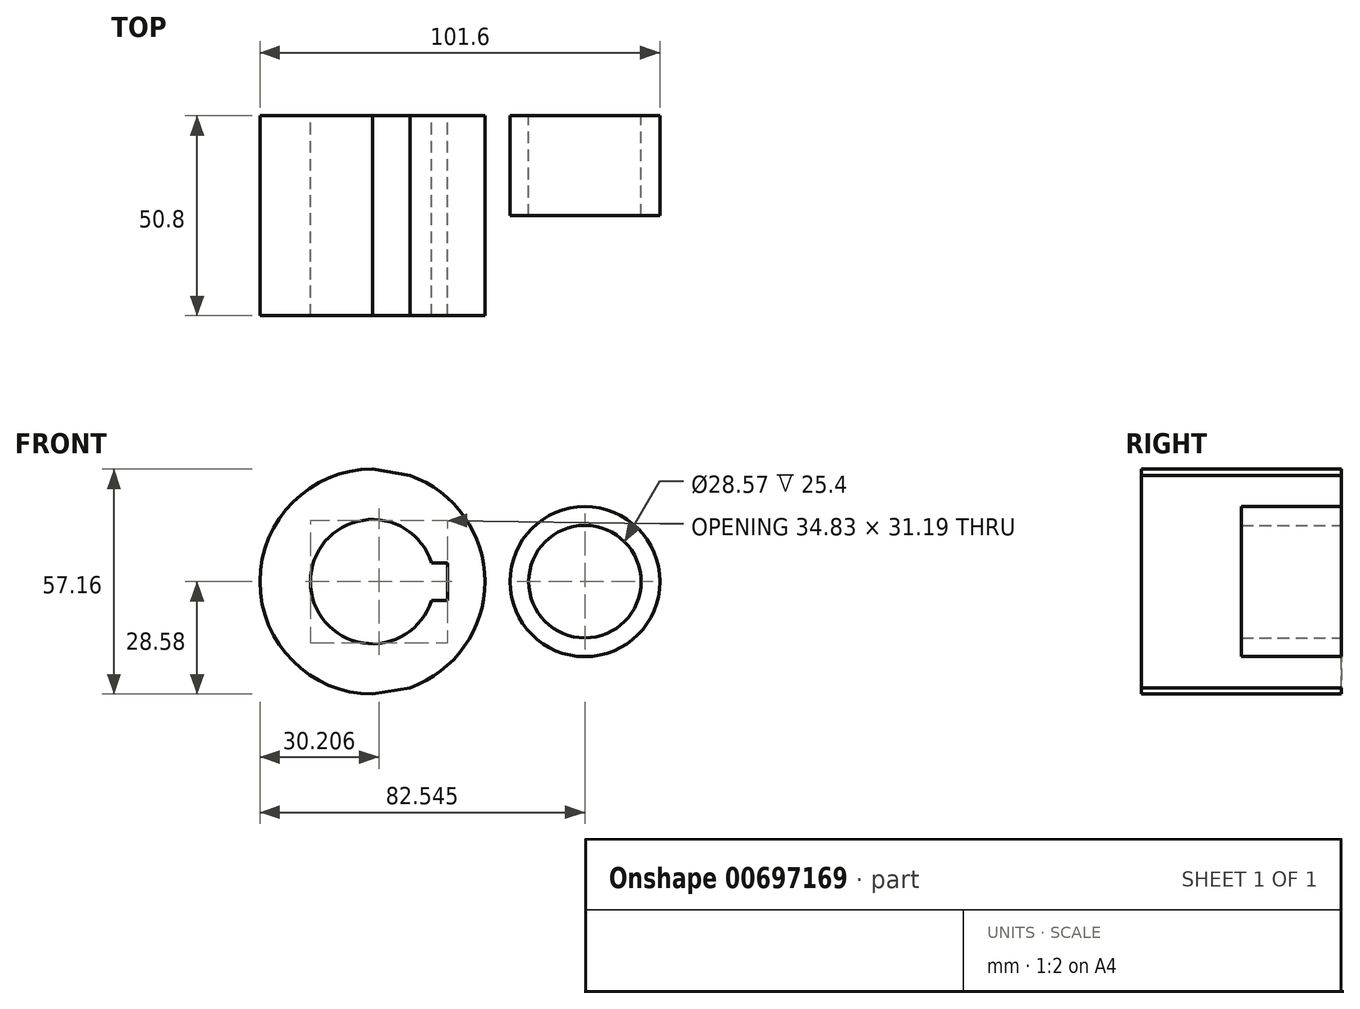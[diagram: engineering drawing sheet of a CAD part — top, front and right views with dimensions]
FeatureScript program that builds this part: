
annotation { "Feature Type Name" : "Feature", "Feature Type Description" : "" }
export const myFeature = defineFeature(function(context is Context, id is Id, definition is map)
    precondition{}
    {
        {
            var Q0;
            Q0=qCreatedBy(makeId("Front.planeOp"),FACE);
            var sketch = newSketch(context, id + "F0", { "sketchPlane" : qUnion([Q0])});
            skCircle(sketch, "E0", {"center": v(0, 0) * mm, "radius": 28.58 * mm});
            skCircle(sketch, "E1", {"center": v(53.97, 0) * mm, "radius": 19.05 * mm});
            skLineSegment(sketch, "E2", {"start": v(0, 28.57) * mm, "end": v(57.2, 18.78) * mm});
            skLineSegment(sketch, "E3", {"start": v(0, -28.58) * mm, "end": v(57.2, -18.78) * mm});
            skCircle(sketch, "E4", {"center": v(0, 0) * mm, "radius": 15.78 * mm});
            skCircle(sketch, "E5", {"center": v(53.97, 0) * mm, "radius": 14.29 * mm});
            skLineSegment(sketch, "E6.bottom", {"start": v(-19.05, -4.76) * mm, "end": v(19.05, -4.76) * mm});
            skLineSegment(sketch, "E6.top", {"start": v(-19.05, 4.76) * mm, "end": v(19.05, 4.76) * mm});
            skLineSegment(sketch, "E6.left", {"start": v(-19.05, -4.76) * mm, "end": v(-19.05, 4.76) * mm});
            skLineSegment(sketch, "E6.right", {"start": v(19.05, -4.76) * mm, "end": v(19.05, 4.76) * mm});
            skSolve(sketch);
        }
        {
            var Q0;
            {var subQ4=sQuery(id+"F0.wireOp",EDGE,"E6.left");Q0=makeQuery(id+"F0.imprint","IMPRINT",FACE,{"disambiguationData":[TD([[makeQuery(id+"F0.imprint","IMPRINT",EDGE,{"derivedFrom":subQ4}),1.0]])]});}
            var Q1;
            {var subQ0=sQuery(id+"F0.wireOp",EDGE,"E2");var subQ1=sQuery(id+"F0.wireOp",EDGE,"E0");var subQ2=makeQuery(id+"F0.imprint","INTERSECT",VERTEX,{"disambiguationData":[OD(1.0)],"derivedFrom":[subQ1,subQ0]});Q1=makeQuery(id+"F0.imprint","IMPRINT",FACE,{"disambiguationData":[TD([[makeQuery(id+"F0.imprint","IMPRINT",EDGE,{"disambiguationData":[TD([[subQ2,1.0]])],"derivedFrom":subQ1}),-1.0]])]});}
            var Q2;
            Q2=makeQuery(id+"F0.imprint","IMPRINT",FACE,{"disambiguationData":[TD([[makeQuery(id+"F0.imprint","IMPRINT",EDGE,{"derivedFrom":sQuery(id+"F0.wireOp",EDGE,"E5")}),-1.0]])]});
            var Q3;
            {var subQ5=sQuery(id+"F0.wireOp",EDGE,"E6.left");Q3=makeQuery(id+"F0.imprint","IMPRINT",FACE,{"disambiguationData":[TD([[makeQuery(id+"F0.imprint","IMPRINT",EDGE,{"derivedFrom":subQ5}),-1.0]])]});}
            extrude(context, id + "F1", {"entities" : qUnion([Q0, Q1, Q2, Q3]), "depth" : 25.4 * mm, "offsetDistance" : 25.4 * mm});
        }
        {
            var Q0;
            {var subQ4=sQuery(id+"F0.wireOp",EDGE,"E6.left");Q0=makeQuery(id+"F0.imprint","IMPRINT",FACE,{"disambiguationData":[TD([[makeQuery(id+"F0.imprint","IMPRINT",EDGE,{"derivedFrom":subQ4}),1.0]])]});}
            var Q1;
            {var subQ5=sQuery(id+"F0.wireOp",EDGE,"E6.left");Q1=makeQuery(id+"F0.imprint","IMPRINT",FACE,{"disambiguationData":[TD([[makeQuery(id+"F0.imprint","IMPRINT",EDGE,{"derivedFrom":subQ5}),-1.0]])]});}
            extrude(context, id + "F2", {"entities" : qUnion([Q0, Q1]), "operationType" : NewBodyOperationType.ADD, "depth" : 50.8 * mm, "offsetDistance" : 25.4 * mm});
        }
    });
